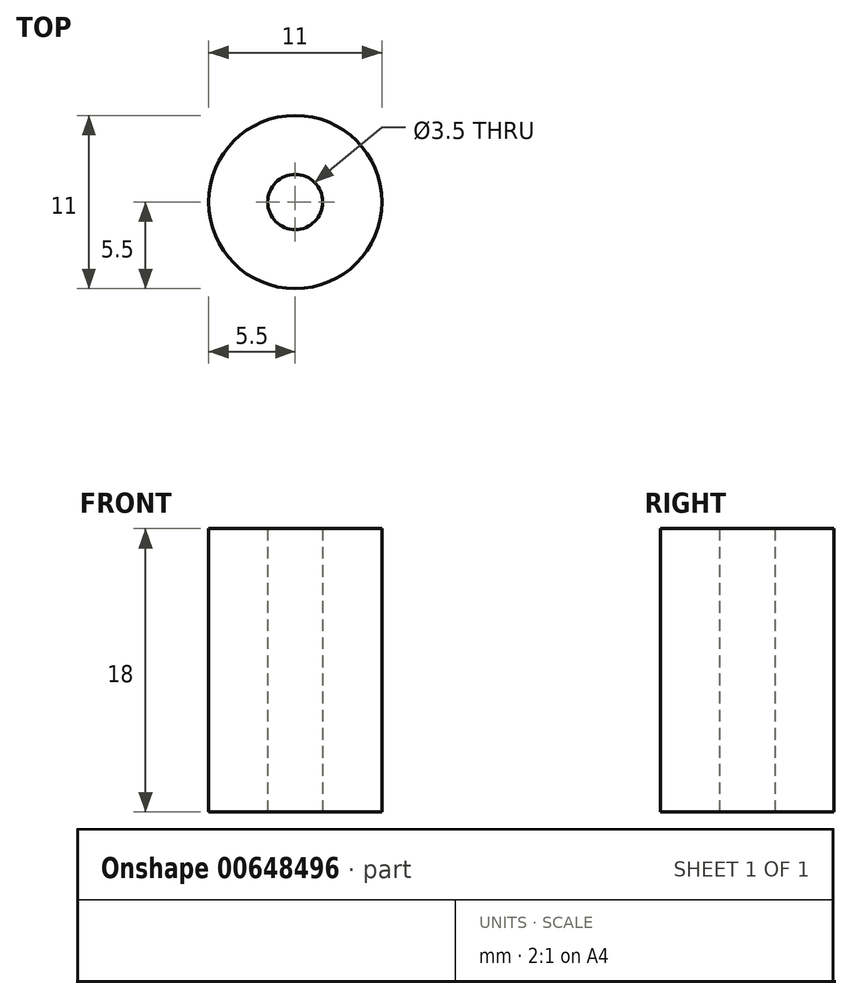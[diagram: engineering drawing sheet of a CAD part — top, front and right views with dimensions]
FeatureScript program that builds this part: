
annotation { "Feature Type Name" : "Feature", "Feature Type Description" : "" }
export const myFeature = defineFeature(function(context is Context, id is Id, definition is map)
    precondition{}
    {
        {
            var Q0;
            Q0=qCreatedBy(makeId("Top.planeOp"),FACE);
            var sketch = newSketch(context, id + "F0", { "sketchPlane" : qUnion([Q0])});
            skCircle(sketch, "E0", {"center": v(0, 0) * mm, "radius": 5.5 * mm});
            skCircle(sketch, "E1", {"center": v(0, 0) * mm, "radius": 1.75 * mm});
            skSolve(sketch);
        }
        {
            var Q0;
            Q0=makeQuery(id+"F0.imprint","IMPRINT",FACE,{"disambiguationData":[TD([[makeQuery(id+"F0.imprint","IMPRINT",EDGE,{"derivedFrom":sQuery(id+"F0.wireOp",EDGE,"E0")}),1.0]])]});
            extrude(context, id + "F1", {"entities" : qUnion([Q0]), "depth" : 18 * mm, "offsetDistance" : 25 * mm});
        }
    });
